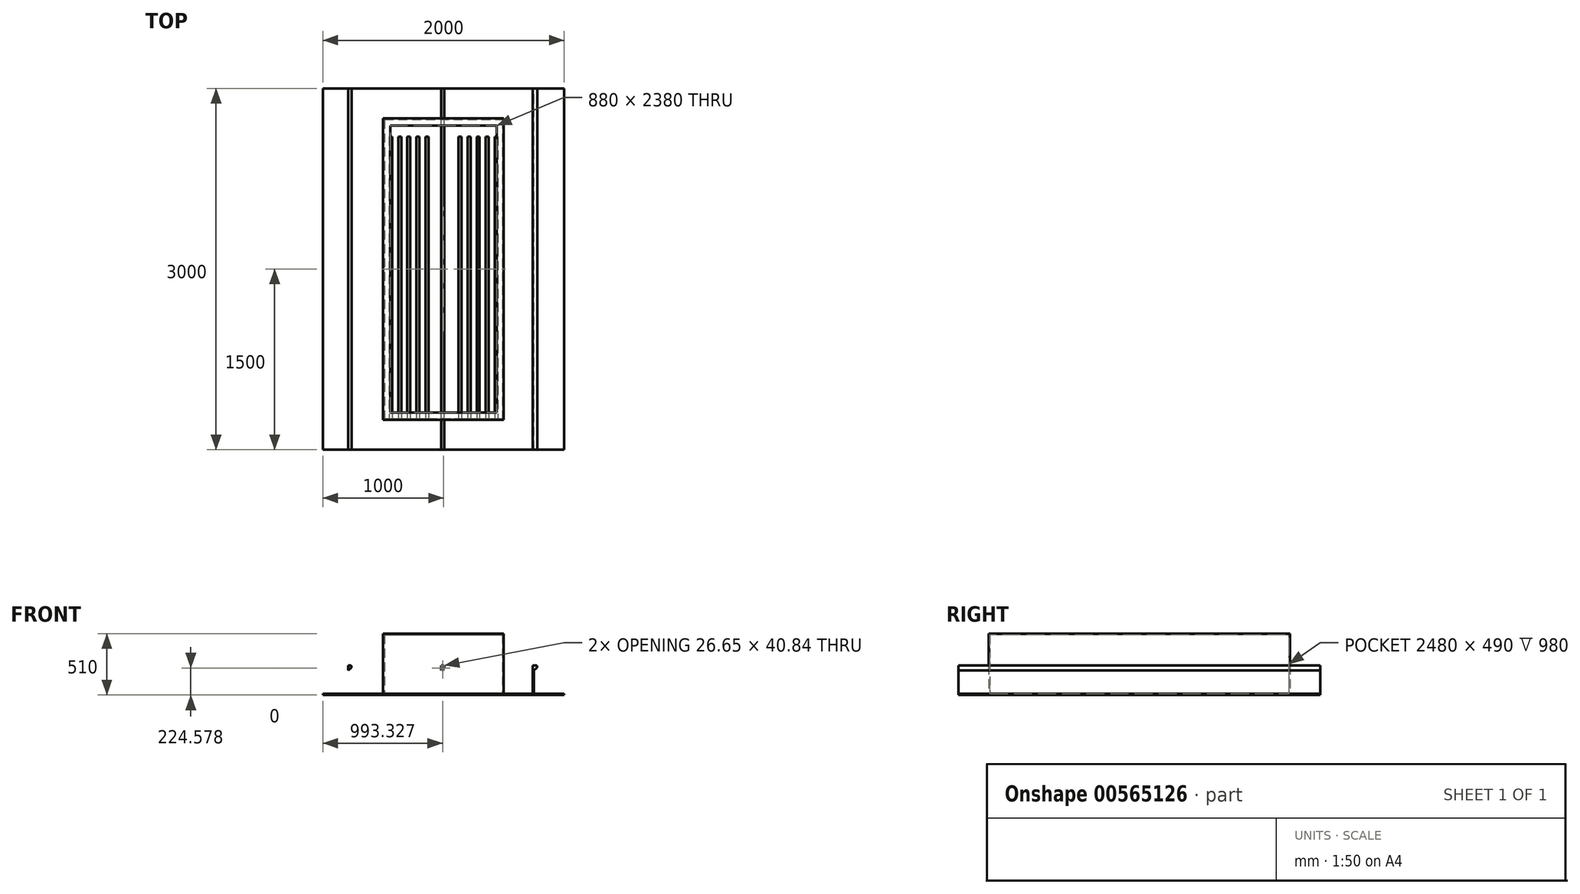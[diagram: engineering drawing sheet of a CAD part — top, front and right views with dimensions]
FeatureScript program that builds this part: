
annotation { "Feature Type Name" : "Feature", "Feature Type Description" : "" }
export const myFeature = defineFeature(function(context is Context, id is Id, definition is map)
    precondition{}
    {
        {
            var Q0;
            Q0=qCreatedBy(makeId("Front.planeOp"),FACE);
            var sketch = newSketch(context, id + "F0", { "sketchPlane" : qUnion([Q0])});
            skLineSegment(sketch, "E0.bottom", {"start": v(-1000, -100) * mm, "end": v(1000, -100) * mm});
            skLineSegment(sketch, "E0.top", {"start": v(-1000, -110) * mm, "end": v(1000, -110) * mm});
            skLineSegment(sketch, "E0.left", {"start": v(-1000, -100) * mm, "end": v(-1000, -110) * mm});
            skLineSegment(sketch, "E0.right", {"start": v(1000, -100) * mm, "end": v(1000, -110) * mm});
            skLineSegment(sketch, "E1.bottom", {"start": v(-800, -100) * mm, "end": v(-790, -100) * mm});
            skLineSegment(sketch, "E1.top", {"start": v(-800, 135) * mm, "end": v(-790, 135) * mm});
            skLineSegment(sketch, "E1.left", {"start": v(-800, -100) * mm, "end": v(-800, 135) * mm});
            skLineSegment(sketch, "E1.right", {"start": v(-790, -100) * mm, "end": v(-790, 135) * mm});
            skLineSegment(sketch, "E2.bottom", {"start": v(-30, -100) * mm, "end": v(-20, -100) * mm});
            skLineSegment(sketch, "E2.top", {"start": v(-30, 135) * mm, "end": v(-20, 135) * mm});
            skLineSegment(sketch, "E2.left", {"start": v(-30, -100) * mm, "end": v(-30, 135) * mm});
            skLineSegment(sketch, "E2.right", {"start": v(-20, -100) * mm, "end": v(-20, 135) * mm});
            skLineSegment(sketch, "E3", {"start": v(-790, 135) * mm, "end": v(-773.3, 135) * mm});
            skLineSegment(sketch, "E4", {"start": v(-20, 135) * mm, "end": v(-3.3, 135) * mm});
            skLineSegment(sketch, "E5", {"start": v(3.77, 117.93) * mm, "end": v(-20, 94.16) * mm});
            skPoint(sketch, "E6.visualSharp", {"position": v(-85.35, 135) * mm});
            skArc(sketch, "E6.filletArc", {"start": v(-766.23, 117.93) * mm, "mid": v(-764.06, 128.83) * mm, "end": v(-773.3, 135) * mm});
            skLineSegment(sketch, "E7", {"start": v(-766.23, 117.93) * mm, "end": v(-790, 94.16) * mm});
            skPoint(sketch, "E8.visualSharp", {"position": v(20.84, 135) * mm});
            skArc(sketch, "E8.filletArc", {"start": v(3.77, 117.93) * mm, "mid": v(5.94, 128.83) * mm, "end": v(-3.3, 135) * mm});
            skLineSegment(sketch, "E9", {"start": v(740, -100) * mm, "end": v(740, 135) * mm});
            skLineSegment(sketch, "E10", {"start": v(740, 135) * mm, "end": v(750, 135) * mm});
            skLineSegment(sketch, "E11", {"start": v(750, 135) * mm, "end": v(766.7, 135) * mm});
            skLineSegment(sketch, "E12", {"start": v(773.77, 117.93) * mm, "end": v(750, 94.16) * mm});
            skPoint(sketch, "E13.visualSharp", {"position": v(790.84, 135) * mm});
            skArc(sketch, "E13.filletArc", {"start": v(773.77, 117.93) * mm, "mid": v(775.94, 128.83) * mm, "end": v(766.7, 135) * mm});
            skLineSegment(sketch, "E14", {"start": v(750, 135) * mm, "end": v(750, -100) * mm});
            skSolve(sketch);
        }
        {
            var Q0;
            {var subQ0=sQuery(id+"F0.wireOp",EDGE,"E3");Q0=makeQuery(id+"F0.imprint","IMPRINT",FACE,{"disambiguationData":[TD([[makeQuery(id+"F0.imprint","IMPRINT",EDGE,{"derivedFrom":subQ0}),-1.0]])]});}
            var Q1;
            {var subQ1=sQuery(id+"F0.wireOp",EDGE,"E1.bottom");Q1=makeQuery(id+"F0.imprint","IMPRINT",FACE,{"disambiguationData":[TD([[makeQuery(id+"F0.imprint","IMPRINT",EDGE,{"derivedFrom":subQ1}),1.0]])]});}
            var Q2;
            Q2=makeQuery(id+"F0.imprint","IMPRINT",FACE,{"disambiguationData":[TD([[makeQuery(id+"F0.imprint","IMPRINT",EDGE,{"derivedFrom":sQuery(id+"F0.wireOp",EDGE,"E0.top")}),1.0]])]});
            var Q3;
            {var subQ1=sQuery(id+"F0.wireOp",EDGE,"E2.bottom");Q3=makeQuery(id+"F0.imprint","IMPRINT",FACE,{"disambiguationData":[TD([[makeQuery(id+"F0.imprint","IMPRINT",EDGE,{"derivedFrom":subQ1}),1.0]])]});}
            var Q4;
            {var subQ0=sQuery(id+"F0.wireOp",EDGE,"E4");Q4=makeQuery(id+"F0.imprint","IMPRINT",FACE,{"disambiguationData":[TD([[makeQuery(id+"F0.imprint","IMPRINT",EDGE,{"derivedFrom":subQ0}),-1.0]])]});}
            var Q5;
            {var subQ0=sQuery(id+"F0.wireOp",EDGE,"E11");Q5=makeQuery(id+"F0.imprint","IMPRINT",FACE,{"disambiguationData":[TD([[makeQuery(id+"F0.imprint","IMPRINT",EDGE,{"derivedFrom":subQ0}),-1.0]])]});}
            var Q6;
            {var subQ1=sQuery(id+"F0.wireOp",EDGE,"E9");Q6=makeQuery(id+"F0.imprint","IMPRINT",FACE,{"disambiguationData":[TD([[makeQuery(id+"F0.imprint","IMPRINT",EDGE,{"derivedFrom":subQ1}),-1.0]])]});}
            extrude(context, id + "F1", {"entities" : qUnion([Q0, Q1, Q2, Q3, Q4, Q5, Q6]), "depth" : 3000 * mm, "offsetDistance" : 25 * mm});
        }
        {
            var Q0;
            {var subQ0=sQuery(id+"F0.wireOp",EDGE,"E0.bottom");Q0=makeQuery(id+"F1.opExtrude","SWEPT_FACE",FACE,{"disambiguationData":[OSD([subQ0]),TDD([makeQuery(id+"F0.imprint","IMPRINT",EDGE,{"disambiguationData":[TD([[makeQuery(id+"F0.imprint","INTERSECT",VERTEX,{"derivedFrom":[subQ0,sQuery(id+"F0.wireOp",EDGE,"E1.bottom"),sQuery(id+"F0.wireOp",EDGE,"E1.right")]}),-1.0]])],"derivedFrom":subQ0})])]});}
            var sketch = newSketch(context, id + "F2", { "sketchPlane" : qUnion([Q0])});
            skLineSegment(sketch, "E15.bottom", {"start": v(-500, -250) * mm, "end": v(500, -250) * mm});
            skLineSegment(sketch, "E15.top", {"start": v(-500, -2750) * mm, "end": v(500, -2750) * mm});
            skLineSegment(sketch, "E15.left", {"start": v(-500, -250) * mm, "end": v(-500, -2750) * mm});
            skLineSegment(sketch, "E15.right", {"start": v(500, -250) * mm, "end": v(500, -2750) * mm});
            skLineSegment(sketch, "E16.bottom", {"start": v(-490, -260) * mm, "end": v(490, -260) * mm});
            skLineSegment(sketch, "E16.top", {"start": v(-490, -2740) * mm, "end": v(490, -2740) * mm});
            skLineSegment(sketch, "E16.left", {"start": v(-490, -260) * mm, "end": v(-490, -2740) * mm});
            skLineSegment(sketch, "E16.right", {"start": v(490, -260) * mm, "end": v(490, -2740) * mm});
            skSolve(sketch);
        }
        {
            var Q0;
            {var subQ6=sQuery(id+"F2.wireOp",EDGE,"E15.left");Q0=makeQuery(id+"F2.imprint","IMPRINT",FACE,{"disambiguationData":[TD([[makeQuery(id+"F2.imprint","IMPRINT",EDGE,{"derivedFrom":subQ6}),1.0]])]});}
            var Q1;
            {var subQ8=sQuery(id+"F2.wireOp",EDGE,"E15.right");Q1=makeQuery(id+"F2.imprint","IMPRINT",FACE,{"disambiguationData":[TD([[makeQuery(id+"F2.imprint","IMPRINT",EDGE,{"derivedFrom":subQ8}),-1.0]])]});}
            extrude(context, id + "F3", {"entities" : qUnion([Q0, Q1]), "operationType" : NewBodyOperationType.ADD, "depth" : 500 * mm, "offsetDistance" : 25 * mm});
        }
        {
            var Q0;
            {var subQ1=sQuery(id+"F0.wireOp",EDGE,"E0.bottom");Q0=makeQuery(id+"F3.boolean.opBoolean","SPLIT",FACE,{"disambiguationData":[TD([makeQuery(id+"F3.opExtrude","SWEPT_FACE",FACE,{"disambiguationData":[OSD([sQuery(id+"F2.wireOp",EDGE,"E16.bottom")])]})])],"derivedFrom":makeQuery(id+"F1.opExtrude","SWEPT_FACE",FACE,{"disambiguationData":[OSD([subQ1]),TDD([makeQuery(id+"F0.imprint","IMPRINT",EDGE,{"disambiguationData":[TD([[makeQuery(id+"F0.imprint","INTERSECT",VERTEX,{"derivedFrom":[subQ1,sQuery(id+"F0.wireOp",EDGE,"E1.bottom"),sQuery(id+"F0.wireOp",EDGE,"E1.right")]}),-1.0]])],"derivedFrom":subQ1})])]})});}
            var sketch = newSketch(context, id + "F4", { "sketchPlane" : qUnion([Q0])});
            skLineSegment(sketch, "E17.bottom", {"start": v(-150, -400) * mm, "end": v(-125, -400) * mm});
            skLineSegment(sketch, "E17.top", {"start": v(-150, -2800) * mm, "end": v(-125, -2800) * mm});
            skLineSegment(sketch, "E17.left", {"start": v(-150, -400) * mm, "end": v(-150, -2800) * mm});
            skLineSegment(sketch, "E17.right", {"start": v(-125, -400) * mm, "end": v(-125, -2800) * mm});
            skLineSegment(sketch, "E18.bottom", {"start": v(-200, -400) * mm, "end": v(-225, -400) * mm});
            skLineSegment(sketch, "E18.top", {"start": v(-200, -2800) * mm, "end": v(-225, -2800) * mm});
            skLineSegment(sketch, "E18.left", {"start": v(-200, -400) * mm, "end": v(-200, -2800) * mm});
            skLineSegment(sketch, "E18.right", {"start": v(-225, -400) * mm, "end": v(-225, -2800) * mm});
            skLineSegment(sketch, "E19.bottom", {"start": v(-275, -400) * mm, "end": v(-300, -400) * mm});
            skLineSegment(sketch, "E19.top", {"start": v(-275, -2800) * mm, "end": v(-300, -2800) * mm});
            skLineSegment(sketch, "E19.left", {"start": v(-275, -400) * mm, "end": v(-275, -2800) * mm});
            skLineSegment(sketch, "E19.right", {"start": v(-300, -400) * mm, "end": v(-300, -2800) * mm});
            skLineSegment(sketch, "E20.bottom", {"start": v(-350, -400) * mm, "end": v(-375, -400) * mm});
            skLineSegment(sketch, "E20.top", {"start": v(-350, -2800) * mm, "end": v(-375, -2800) * mm});
            skLineSegment(sketch, "E20.left", {"start": v(-350, -400) * mm, "end": v(-350, -2800) * mm});
            skLineSegment(sketch, "E20.right", {"start": v(-375, -400) * mm, "end": v(-375, -2800) * mm});
            skLineSegment(sketch, "E21.bottom", {"start": v(-425, -400) * mm, "end": v(-450, -400) * mm});
            skLineSegment(sketch, "E21.top", {"start": v(-425, -2800) * mm, "end": v(-450, -2800) * mm});
            skLineSegment(sketch, "E21.left", {"start": v(-425, -400) * mm, "end": v(-425, -2800) * mm});
            skLineSegment(sketch, "E21.right", {"start": v(-450, -400) * mm, "end": v(-450, -2800) * mm});
            skLineSegment(sketch, "E22.bottom", {"start": v(125, -400) * mm, "end": v(150, -400) * mm});
            skLineSegment(sketch, "E22.top", {"start": v(125, -2800) * mm, "end": v(150, -2800) * mm});
            skLineSegment(sketch, "E22.left", {"start": v(125, -400) * mm, "end": v(125, -2800) * mm});
            skLineSegment(sketch, "E22.right", {"start": v(150, -400) * mm, "end": v(150, -2800) * mm});
            skLineSegment(sketch, "E23.bottom", {"start": v(200, -400) * mm, "end": v(225, -400) * mm});
            skLineSegment(sketch, "E23.top", {"start": v(200, -2800) * mm, "end": v(225, -2800) * mm});
            skLineSegment(sketch, "E23.left", {"start": v(200, -400) * mm, "end": v(200, -2800) * mm});
            skLineSegment(sketch, "E23.right", {"start": v(225, -400) * mm, "end": v(225, -2800) * mm});
            skLineSegment(sketch, "E24.bottom", {"start": v(275, -400) * mm, "end": v(300, -400) * mm});
            skLineSegment(sketch, "E24.top", {"start": v(275, -2800) * mm, "end": v(300, -2800) * mm});
            skLineSegment(sketch, "E24.left", {"start": v(275, -400) * mm, "end": v(275, -2800) * mm});
            skLineSegment(sketch, "E24.right", {"start": v(300, -400) * mm, "end": v(300, -2800) * mm});
            skLineSegment(sketch, "E25.bottom", {"start": v(350, -400) * mm, "end": v(375, -400) * mm});
            skLineSegment(sketch, "E25.top", {"start": v(350, -2800) * mm, "end": v(375, -2800) * mm});
            skLineSegment(sketch, "E25.left", {"start": v(350, -400) * mm, "end": v(350, -2800) * mm});
            skLineSegment(sketch, "E25.right", {"start": v(375, -400) * mm, "end": v(375, -2800) * mm});
            skLineSegment(sketch, "E26.bottom", {"start": v(425, -400) * mm, "end": v(450, -400) * mm});
            skLineSegment(sketch, "E26.top", {"start": v(425, -2800) * mm, "end": v(450, -2800) * mm});
            skLineSegment(sketch, "E26.left", {"start": v(425, -400) * mm, "end": v(425, -2800) * mm});
            skLineSegment(sketch, "E26.right", {"start": v(450, -400) * mm, "end": v(450, -2800) * mm});
            skSolve(sketch);
        }
        {
            var Q0;
            Q0=makeQuery(id+"F4.imprint","IMPRINT",FACE,{"disambiguationData":[TD([[makeQuery(id+"F4.imprint","IMPRINT",EDGE,{"derivedFrom":sQuery(id+"F4.wireOp",EDGE,"E21.bottom")}),1.0]])]});
            var Q1;
            Q1=makeQuery(id+"F4.imprint","IMPRINT",FACE,{"disambiguationData":[TD([[makeQuery(id+"F4.imprint","IMPRINT",EDGE,{"derivedFrom":sQuery(id+"F4.wireOp",EDGE,"E20.bottom")}),1.0]])]});
            var Q2;
            Q2=makeQuery(id+"F4.imprint","IMPRINT",FACE,{"disambiguationData":[TD([[makeQuery(id+"F4.imprint","IMPRINT",EDGE,{"derivedFrom":sQuery(id+"F4.wireOp",EDGE,"E19.bottom")}),1.0]])]});
            var Q3;
            Q3=makeQuery(id+"F4.imprint","IMPRINT",FACE,{"disambiguationData":[TD([[makeQuery(id+"F4.imprint","IMPRINT",EDGE,{"derivedFrom":sQuery(id+"F4.wireOp",EDGE,"E18.bottom")}),1.0]])]});
            var Q4;
            Q4=makeQuery(id+"F4.imprint","IMPRINT",FACE,{"disambiguationData":[TD([[makeQuery(id+"F4.imprint","IMPRINT",EDGE,{"derivedFrom":sQuery(id+"F4.wireOp",EDGE,"E17.bottom")}),-1.0]])]});
            var Q5;
            Q5=makeQuery(id+"F4.imprint","IMPRINT",FACE,{"disambiguationData":[TD([[makeQuery(id+"F4.imprint","IMPRINT",EDGE,{"derivedFrom":sQuery(id+"F4.wireOp",EDGE,"E22.bottom")}),-1.0]])]});
            var Q6;
            Q6=makeQuery(id+"F4.imprint","IMPRINT",FACE,{"disambiguationData":[TD([[makeQuery(id+"F4.imprint","IMPRINT",EDGE,{"derivedFrom":sQuery(id+"F4.wireOp",EDGE,"E23.bottom")}),-1.0]])]});
            var Q7;
            Q7=makeQuery(id+"F4.imprint","IMPRINT",FACE,{"disambiguationData":[TD([[makeQuery(id+"F4.imprint","IMPRINT",EDGE,{"derivedFrom":sQuery(id+"F4.wireOp",EDGE,"E24.bottom")}),-1.0]])]});
            var Q8;
            Q8=makeQuery(id+"F4.imprint","IMPRINT",FACE,{"disambiguationData":[TD([[makeQuery(id+"F4.imprint","IMPRINT",EDGE,{"derivedFrom":sQuery(id+"F4.wireOp",EDGE,"E25.bottom")}),-1.0]])]});
            var Q9;
            Q9=makeQuery(id+"F4.imprint","IMPRINT",FACE,{"disambiguationData":[TD([[makeQuery(id+"F4.imprint","IMPRINT",EDGE,{"derivedFrom":sQuery(id+"F4.wireOp",EDGE,"E26.bottom")}),-1.0]])]});
            extrude(context, id + "F5", {"entities" : qUnion([Q0, Q1, Q2, Q3, Q4, Q5, Q6, Q7, Q8, Q9]), "operationType" : NewBodyOperationType.REMOVE, "oppositeDirection" : true, "depth" : 10 * mm, "offsetDistance" : 25 * mm});
        }
        {
            var Q0;
            Q0=makeQuery(id+"F3.opExtrude","CAP_FACE",FACE,{"disambiguationData":[OSD([sQuery(id+"F2.wireOp",EDGE,"E15.bottom"),sQuery(id+"F2.wireOp",EDGE,"E15.top"),sQuery(id+"F2.wireOp",EDGE,"E15.left"),sQuery(id+"F2.wireOp",EDGE,"E15.right"),sQuery(id+"F2.wireOp",EDGE,"E16.bottom"),sQuery(id+"F2.wireOp",EDGE,"E16.top"),sQuery(id+"F2.wireOp",EDGE,"E16.left"),sQuery(id+"F2.wireOp",EDGE,"E16.right")])],"isStart":false});
            var sketch = newSketch(context, id + "F6", { "sketchPlane" : qUnion([Q0])});
            skLineSegment(sketch, "E27.bottom", {"start": v(-490, -260) * mm, "end": v(490, -260) * mm});
            skLineSegment(sketch, "E27.top", {"start": v(-490, -2740) * mm, "end": v(490, -2740) * mm});
            skLineSegment(sketch, "E27.left", {"start": v(-490, -260) * mm, "end": v(-490, -2740) * mm});
            skLineSegment(sketch, "E27.right", {"start": v(490, -260) * mm, "end": v(490, -2740) * mm});
            skLineSegment(sketch, "E28.bottom", {"start": v(-440, -310) * mm, "end": v(440, -310) * mm});
            skLineSegment(sketch, "E28.top", {"start": v(-440, -2690) * mm, "end": v(440, -2690) * mm});
            skLineSegment(sketch, "E28.left", {"start": v(-440, -310) * mm, "end": v(-440, -2690) * mm});
            skLineSegment(sketch, "E28.right", {"start": v(440, -310) * mm, "end": v(440, -2690) * mm});
            skSolve(sketch);
        }
        {
            var Q0;
            Q0=makeQuery(id+"F6.imprint","IMPRINT",FACE,{"disambiguationData":[TD([[makeQuery(id+"F6.imprint","IMPRINT",EDGE,{"derivedFrom":sQuery(id+"F6.wireOp",EDGE,"E27.bottom")}),-1.0]])]});
            extrude(context, id + "F7", {"entities" : qUnion([Q0]), "operationType" : NewBodyOperationType.ADD, "oppositeDirection" : true, "depth" : 10 * mm, "offsetDistance" : 25 * mm});
        }
    });
